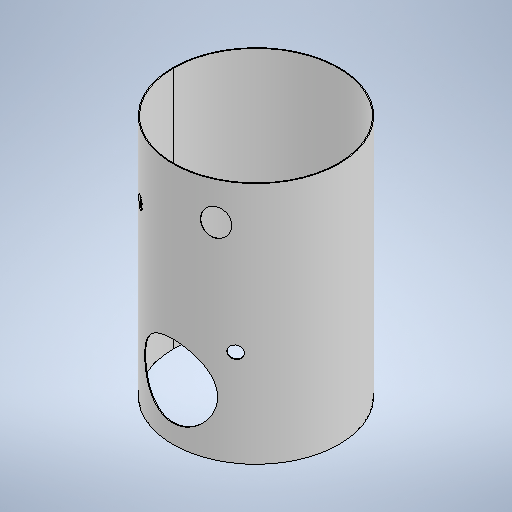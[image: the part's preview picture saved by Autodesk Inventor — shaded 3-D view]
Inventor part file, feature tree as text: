
AUTODESK INVENTOR PART (.ipt)
format: ipt  version: 2025.1 (Build 291241020, 241B)  size: 1,860,096 bytes
history: native  units: mm
features: other x9, sketch x6, extrude x4, revolve x1, plane x1
ambient origin geometry x8: Origin, YZ Plane, XZ Plane, XY Plane, X Axis, Y Axis, Z Axis, Center Point
bodies: Solid1 (feature_tree)
feature tree (21):
  revolve  "Revolution1"  [1 undecoded]
  extrude  "Extrusion1"  Depth=62.8144mm
  other  "floor angle sketch"
  other  "Feeder Plane"
  other  "Feeder horisont hight angle"
  other  "Feeder Work Plane"
  extrude  "Feeder Extrusion"  TaperAngle=0.0deg  [1 undecoded]
  other  "Inner Plane"
  other  "Inner horisont hight angle"
  other  "Inner Work Plane"
  extrude  "Inner Extrusion"  Depth=400.0mm
  other  "Outer Plane"
  sketch  "Sketch11"  dims[d16=400.0mm d17=180.0mm]
  plane  "Work Plane9"
  extrude  "Extrusion6"  Depth=400.0mm
  sketch  "Sketch1"  dims[d0=6.0mm d1=1770.0mm]
  sketch  "Sketch2"  dims[d2=1200.0mm d3=62.8144mm]
  sketch  "Sketch8"  dims[d4=530.0mm d10=0.0mm d11=0.0mm]
  sketch  "Sketch10"  dims[d12=400.0mm d15=200.0mm]
  sketch  "Sketch12"  dims[d34=1500.0mm d35=30.0deg d36=172.0mm d38=10.0mm d39=0.0mm d40=0.0mm d41=1300.0mm d42=91.0mm d43=0.0mm d44=0.0mm d45=0.0mm d46=700.0mm d47=92.0mm d48=10.0mm d49=0.0mm]
  other  "Definition1"
note: 2 required parameter values undecoded (feature->parameter linkage not recoverable at this tier; creation-order binding heuristic only, values carry confidence <= 0.55)